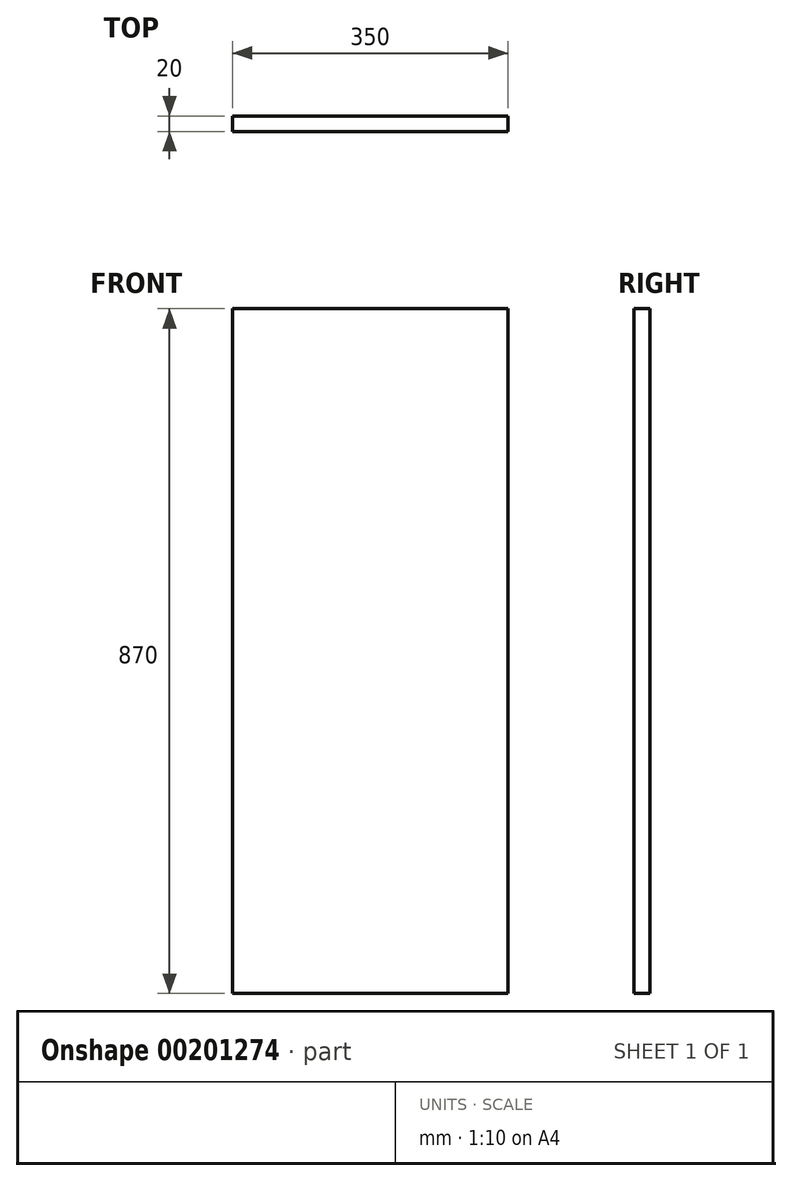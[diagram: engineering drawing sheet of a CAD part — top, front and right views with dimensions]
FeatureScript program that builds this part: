
annotation { "Feature Type Name" : "Feature", "Feature Type Description" : "" }
export const myFeature = defineFeature(function(context is Context, id is Id, definition is map)
    precondition{}
    {
        {
            var Q0;
            Q0=qCreatedBy(makeId("Top.planeOp"),FACE);
            var sketch = newSketch(context, id + "F0", { "sketchPlane" : qUnion([Q0])});
            skLineSegment(sketch, "E0.bottom", {"start": v(0, 0) * mm, "end": v(350, 0) * mm});
            skLineSegment(sketch, "E0.top", {"start": v(0, 20) * mm, "end": v(350, 20) * mm});
            skLineSegment(sketch, "E0.left", {"start": v(0, 0) * mm, "end": v(0, 20) * mm});
            skLineSegment(sketch, "E0.right", {"start": v(350, 0) * mm, "end": v(350, 20) * mm});
            skSolve(sketch);
        }
        {
            var Q0;
            Q0=qSketchRegion(id+"F0",true);
            extrude(context, id + "F1", {"entities" : qUnion([Q0]), "depth" : 870 * mm});
        }
    });
